# Revit family: WASP2
name_source: partatom
category: Lighting Devices
units: mm (PartAtom-declared; Revit-internal decimal feet)

## family parameters
Cut with Voids When Loaded = No
Host = Face
Maintain Annotation Orientation = Yes
OmniClass Number = 23.85.80.11.27
OmniClass Title = Lighting Controls
Part Type = Normal
Room Calculation Point = No
Round Connector Dimension = Use Diameter
Shared = No

## types (1)
- WASP2
    Apparent Load = 0.000 VA
    Assembly Code = D5020
    Certifications = UL STD 508, UL STD 244A
    Connector Description 1 = Power Supply
    Connector Description 2 = Controls
    Coverage = 360°, 180°, Aisle, Half Aisle
    Default Elevation = 48 "
    Description = Occupancy Sensors and Controllers
    Device Material = Plastic -  White
    Electrical Ratings = 120VAC;277VAC;347VAC;480VAC
    Frequency = 60 Hz
    Glass = Plastic -  Glass
    Humidity = 0% to 95%
    Lens Options = Low Mount/High Mount
    Load Classification = Lighting
    Manufacturer = NX Lighting Controls
    Model = WASP2
    Number of Poles = 1
    Operating Environment = Standard Version and LWO(Low-Temp/Water Tight/Indoor/Outdoor)
    Operating Temperature = Indoor : 32° to 149°F (0° to 65°C); Outdoor version: -40° to 149°F (-40° to 65°C)
    Power Factor = 1
    Timer Timeouts = Primary: 8-second test mode - 4, 8, 16 and 30 minute timeouts; Secondary: Can be disable - 30, 60 and 90 minute timeouts
    Type Comments = Lighting Device
    URL = https://www.currentlighting.com
    Voltage = 120 V
    Warranty = Five-year limited
    Wattage = 800 W
    Weight = 0.20 kg

## geometry (parser evidence)
native form markers: Blend x4, Sweep x6
no freeform markers — native parametric forms only
